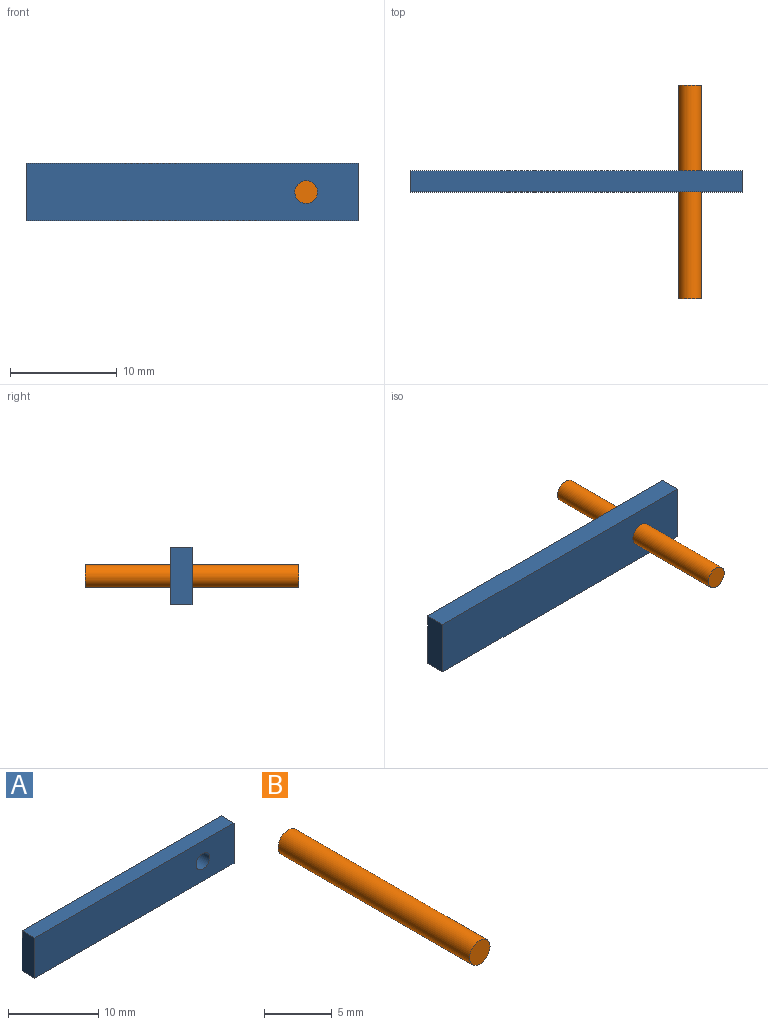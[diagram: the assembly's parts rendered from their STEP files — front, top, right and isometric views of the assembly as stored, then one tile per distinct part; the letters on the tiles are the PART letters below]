
ASSEMBLY  parts=2 mates=1
PART A: 7 faces, bbox 31.2x2x5.4 mm
  f0: plane 5.44x2mm, normal (1,0,0), area 10.9mm2, adj f1,f3,f5,f6
  f1: plane 31.17x2mm, normal (0,0,1), area 62.3mm2, adj f0,f2,f5,f6
  f2: plane 5.44x2mm, normal (-1,0,0), area 10.9mm2, adj f1,f3,f5,f6
  f3: plane 31.17x2mm, normal (0,0,-1), area 62.3mm2, adj f0,f2,f5,f6
  f4: cylinder r=1.07mm len=2.13mm, axis (0,1,0), area 13.4mm2, adj f5,f6
  f5: plane 31.17x5.44mm, normal (0,-1,0), area 165.9mm2, adj f0,f1,f2,f3,f4
  f6: plane 31.17x5.44mm, normal (0,1,0), area 165.9mm2, adj f0,f1,f2,f3,f4
PART B: 3 faces, bbox 2.1x20x2.1 mm
  f0: cylinder r=1.07mm len=20mm, axis (0,1,0), area 134.1mm2, adj f1,f2
  f1: plane 2.13x2.13mm, normal (0,-1,0), area 3.6mm2, adj f0
  f2: plane 2.13x2.13mm, normal (0,1,0), area 3.6mm2, adj f0
PLACE A rot(axis=(0,-1,0),0deg) t=(-10.73,-4.57,0.02)mm
PLACE B t=(-10.73,-5.57,0.02)mm
MATE revolute A.f4 <-> B.f0  axis (0,-1,0) through (-0.01,-5.57,0.02)mm
